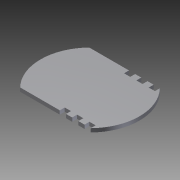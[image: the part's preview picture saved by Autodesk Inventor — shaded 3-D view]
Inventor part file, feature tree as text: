
AUTODESK INVENTOR PART (.ipt)
format: ipt  version: 2012 (Build 160160000, 160)  size: 101,376 bytes
history: native  units: mm
features: extrude x1, sketch x1
ambient origin geometry x8: Origin, YZ Plane, XZ Plane, XY Plane, X Axis, Y Axis, Z Axis, Center Point
bodies: Solid1 (feature_tree)
feature tree (2):
  extrude  "Extrusion1"  Depth=40.0mm
  sketch  "Sketch1"  dims[d0=80.0mm d2=40.0mm d3=40.0mm d4=4.0mm d9=5.0mm d17=4.0mm d18=4.0mm d20=4.0mm d21=4.0mm d22=3.0mm d23=0.0mm]
